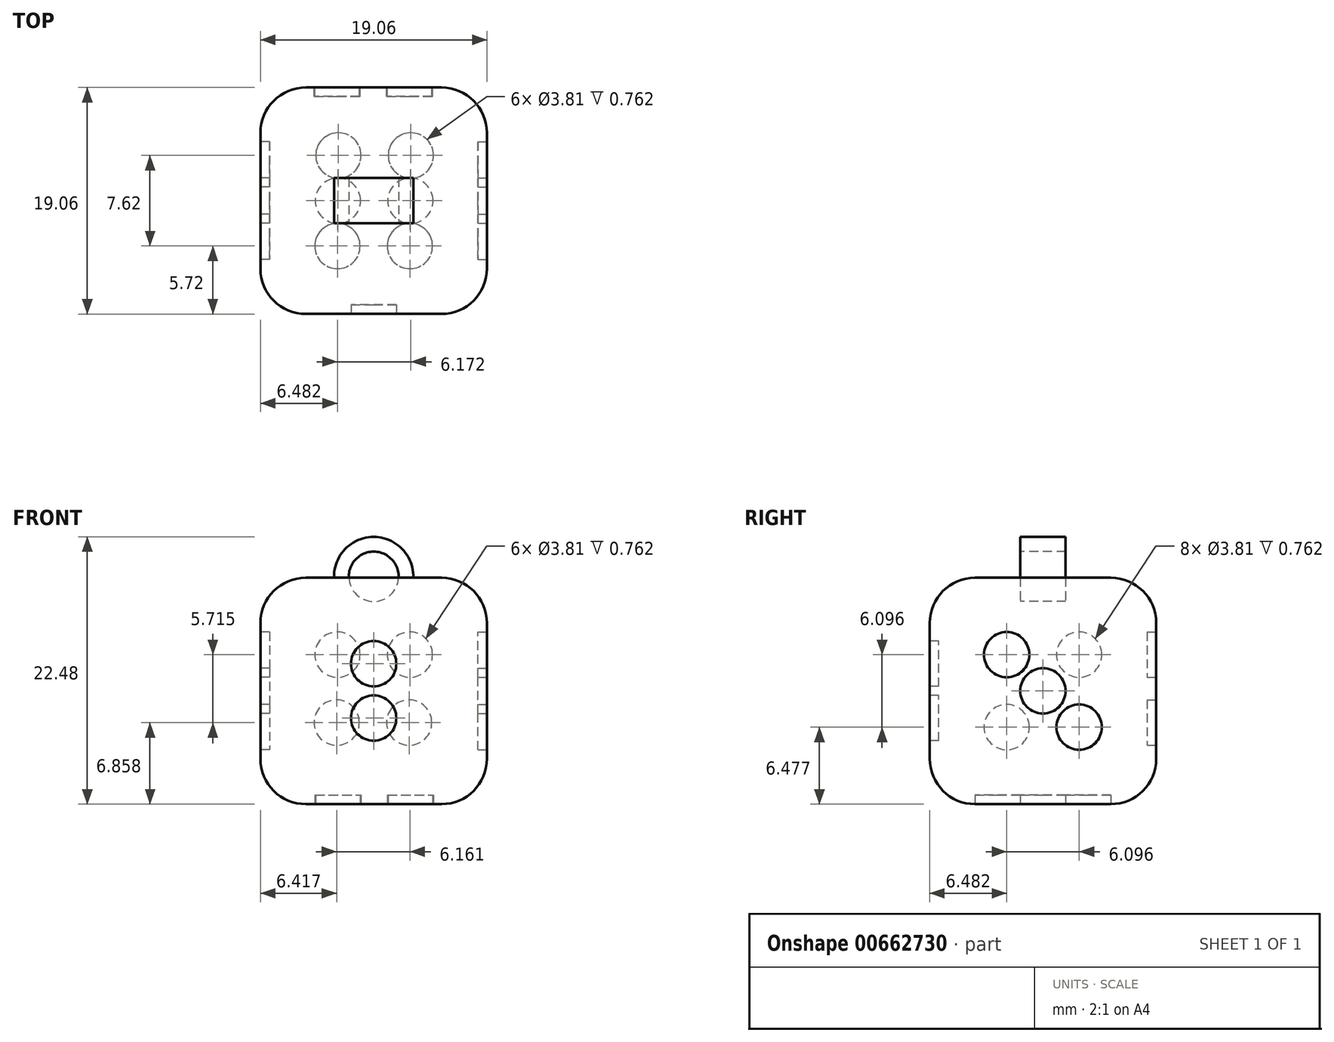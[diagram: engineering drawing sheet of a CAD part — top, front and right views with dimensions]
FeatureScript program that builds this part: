
annotation { "Feature Type Name" : "Feature", "Feature Type Description" : "" }
export const myFeature = defineFeature(function(context is Context, id is Id, definition is map)
    precondition{}
    {
        {
            var Q0;
            Q0=qCreatedBy(makeId("Top.planeOp"),FACE);
            var sketch = newSketch(context, id + "F0", { "sketchPlane" : qUnion([Q0])});
            skLineSegment(sketch, "E0.bottom", {"start": v(6.35, -6.35) * mm, "end": v(-6.35, -6.35) * mm});
            skLineSegment(sketch, "E0.top", {"start": v(6.35, 6.35) * mm, "end": v(-6.35, 6.35) * mm});
            skLineSegment(sketch, "E0.left", {"start": v(6.35, -6.35) * mm, "end": v(6.35, 6.35) * mm});
            skLineSegment(sketch, "E0.right", {"start": v(-6.35, -6.35) * mm, "end": v(-6.35, 6.35) * mm});
            skPoint(sketch, "E0.middle", {"position": v(0, 0) * mm});
            skSolve(sketch);
        }
        {
            var Q0;
            Q0 = qSketchRegion(id + "F0", true);
            extrude(context, id + "F1", {"entities" : qUnion([Q0]), "depth" : 12.7 * mm, "offsetDistance" : 25.4 * mm});
        }
        {
            var Q0;
            Q0=makeQuery(id+"F1.opExtrude","CAP_FACE",FACE,{"disambiguationData":[OSD([sQuery(id+"F0.wireOp",EDGE,"E0.bottom"),sQuery(id+"F0.wireOp",EDGE,"E0.top"),sQuery(id+"F0.wireOp",EDGE,"E0.left"),sQuery(id+"F0.wireOp",EDGE,"E0.right")])],"isStart":false});
            fillet(context, id + "F2", {"entities" : qUnion([Q0]), "radius" : 2.54 * mm, "tangentPropagation" : true, "allowEdgeOverflow" : false});
        }
        {
            var Q0;
            Q0=makeQuery(id+"F1.opExtrude","SWEPT_FACE",FACE,{"disambiguationData":[OSD([sQuery(id+"F0.wireOp",EDGE,"E0.bottom")])]});
            fillet(context, id + "F3", {"entities" : qUnion([Q0]), "radius" : 2.54 * mm, "tangentPropagation" : true, "allowEdgeOverflow" : false});
        }
        {
            var Q0;
            Q0=makeQuery(id+"F1.opExtrude","SWEPT_FACE",FACE,{"disambiguationData":[OSD([sQuery(id+"F0.wireOp",EDGE,"E0.left")])]});
            fillet(context, id + "F4", {"entities" : qUnion([Q0]), "radius" : 2.54 * mm, "tangentPropagation" : true, "allowEdgeOverflow" : false});
        }
        {
            var Q0;
            Q0=makeQuery(id+"F1.opExtrude","SWEPT_FACE",FACE,{"disambiguationData":[OSD([sQuery(id+"F0.wireOp",EDGE,"E0.top")])]});
            fillet(context, id + "F5", {"entities" : qUnion([Q0]), "radius" : 2.54 * mm, "tangentPropagation" : true, "allowEdgeOverflow" : false});
        }
        {
            var Q0;
            Q0=makeQuery(id+"F1.opExtrude","SWEPT_FACE",FACE,{"disambiguationData":[OSD([sQuery(id+"F0.wireOp",EDGE,"E0.right")])]});
            fillet(context, id + "F6", {"entities" : qUnion([Q0]), "radius" : 2.54 * mm, "tangentPropagation" : true, "allowEdgeOverflow" : false});
        }
        {
            var Q0;
            Q0=qCreatedBy(makeId("Front.planeOp"),FACE);
            var sketch = newSketch(context, id + "F7", { "sketchPlane" : qUnion([Q0])});
            skCircle(sketch, "E1", {"center": v(0, 12.76) * mm, "radius": 2.22 * mm});
            skSolve(sketch);
        }
        {
            var Q0;
            Q0 = qSketchRegion(id + "F7", true);
            extrude(context, id + "F8", {"entities" : qUnion([Q0]), "operationType" : NewBodyOperationType.ADD, "endBound" : BoundingType.SYMMETRIC, "depth" : 2.54 * mm, "offsetDistance" : 25.4 * mm});
        }
        {
            var Q0;
            Q0=makeQuery(id+"F8.opExtrude","CAP_FACE",FACE,{"disambiguationData":[OSD([sQuery(id+"F7.wireOp",EDGE,"E1")])],"isStart":false});
            var sketch = newSketch(context, id + "F9", { "sketchPlane" : qUnion([Q0])});
            skCircle(sketch, "E2", {"center": v(0, 12.76) * mm, "radius": 1.4 * mm});
            skSolve(sketch);
        }
        {
            var Q0;
            Q0 = qSketchRegion(id + "F9", true);
            extrude(context, id + "F10", {"entities" : qUnion([Q0]), "operationType" : NewBodyOperationType.REMOVE, "oppositeDirection" : true, "depth" : 2.54 * mm, "offsetDistance" : 25.4 * mm});
        }
        {
            var Q0;
            Q0=makeQuery(id+"F1.opExtrude","SWEPT_FACE",FACE,{"disambiguationData":[OSD([sQuery(id+"F0.wireOp",EDGE,"E0.bottom")])]});
            var sketch = newSketch(context, id + "F11", { "sketchPlane" : qUnion([Q0])});
            skCircle(sketch, "E3", {"center": v(0, 4.83) * mm, "radius": 1.27 * mm});
            skPoint(sketch, "E3.centerSnap0", {"position": v(0, 2.54) * mm});
            skCircle(sketch, "E4", {"center": v(0, 7.87) * mm, "radius": 1.27 * mm});
            skPoint(sketch, "E4.centerSnap0", {"position": v(0, 10.16) * mm});
            skSolve(sketch);
        }
        {
            var Q0;
            Q0 = qSketchRegion(id + "F11", true);
            extrude(context, id + "F12", {"entities" : qUnion([Q0]), "operationType" : NewBodyOperationType.REMOVE, "oppositeDirection" : true, "depth" : 0.5 * mm, "offsetDistance" : 25.4 * mm});
        }
        {
            var Q0;
            Q0=makeQuery(id+"F1.opExtrude","SWEPT_FACE",FACE,{"disambiguationData":[OSD([sQuery(id+"F0.wireOp",EDGE,"E0.left")])]});
            var sketch = newSketch(context, id + "F13", { "sketchPlane" : qUnion([Q0])});
            skLineSegment(sketch, "E5", {"start": v(-3.8, 10.16) * mm, "end": v(3.81, 2.54) * mm});
            skLineSegment(sketch, "E6", {"start": v(-3.8, 2.54) * mm, "end": v(3.81, 10.16) * mm});
            skCircle(sketch, "E7", {"center": v(0, 6.35) * mm, "radius": 1.27 * mm});
            skCircle(sketch, "E8", {"center": v(-2.03, 8.38) * mm, "radius": 1.27 * mm});
            skCircle(sketch, "E9", {"center": v(2.03, 4.32) * mm, "radius": 1.27 * mm});
            skSolve(sketch);
        }
        {
            var Q0;
            Q0 = qSketchRegion(id + "F13", true);
            extrude(context, id + "F14", {"entities" : qUnion([Q0]), "operationType" : NewBodyOperationType.REMOVE, "oppositeDirection" : true, "depth" : 0.5 * mm, "offsetDistance" : 25.4 * mm});
        }
        {
            var Q0;
            Q0=makeQuery(id+"F1.opExtrude","SWEPT_FACE",FACE,{"disambiguationData":[OSD([sQuery(id+"F0.wireOp",EDGE,"E0.top")])]});
            var sketch = newSketch(context, id + "F15", { "sketchPlane" : qUnion([Q0])});
            skCircle(sketch, "E10", {"center": v(-2.03, 8.38) * mm, "radius": 1.27 * mm});
            skCircle(sketch, "E11.1.0.0", {"center": v(2.03, 8.38) * mm, "radius": 1.27 * mm});
            skLineSegment(sketch, "E11.direction1", {"start": v(-2.03, 8.38) * mm, "end": v(2.03, 8.38) * mm, "construction": true});
            skCircle(sketch, "E12.1.0.0", {"center": v(-1.99, 4.57) * mm, "radius": 1.27 * mm});
            skCircle(sketch, "E12.1.0.1", {"center": v(2.08, 4.57) * mm, "radius": 1.27 * mm});
            skLineSegment(sketch, "E12.direction1", {"start": v(-2.03, 8.38) * mm, "end": v(-1.99, 4.57) * mm, "construction": true});
            skSolve(sketch);
        }
        {
            var Q0;
            Q0 = qSketchRegion(id + "F15", true);
            extrude(context, id + "F16", {"entities" : qUnion([Q0]), "operationType" : NewBodyOperationType.REMOVE, "oppositeDirection" : true, "depth" : 0.5 * mm, "offsetDistance" : 25.4 * mm});
        }
        {
            var Q0;
            Q0=makeQuery(id+"F1.opExtrude","SWEPT_FACE",FACE,{"disambiguationData":[OSD([sQuery(id+"F0.wireOp",EDGE,"E0.right")])]});
            var sketch = newSketch(context, id + "F17", { "sketchPlane" : qUnion([Q0])});
            skLineSegment(sketch, "E13", {"start": v(-3.81, 10.16) * mm, "end": v(3.8, 2.54) * mm});
            skLineSegment(sketch, "E14", {"start": v(-3.81, 2.54) * mm, "end": v(3.81, 10.16) * mm});
            skCircle(sketch, "E15", {"center": v(0, 6.35) * mm, "radius": 1.27 * mm});
            skCircle(sketch, "E16", {"center": v(-2.03, 8.38) * mm, "radius": 1.27 * mm});
            skCircle(sketch, "E17.1.0.0", {"center": v(2.03, 8.38) * mm, "radius": 1.27 * mm});
            skLineSegment(sketch, "E17.direction1", {"start": v(-2.03, 8.38) * mm, "end": v(2.03, 8.38) * mm, "construction": true});
            skCircle(sketch, "E18", {"center": v(-2.03, 4.32) * mm, "radius": 1.27 * mm});
            skCircle(sketch, "E19.1.0.0", {"center": v(2.03, 4.32) * mm, "radius": 1.27 * mm});
            skLineSegment(sketch, "E19.direction1", {"start": v(-2.03, 4.32) * mm, "end": v(2.03, 4.32) * mm, "construction": true});
            skSolve(sketch);
        }
        {
            var Q0;
            Q0 = qSketchRegion(id + "F17", true);
            extrude(context, id + "F18", {"entities" : qUnion([Q0]), "operationType" : NewBodyOperationType.REMOVE, "oppositeDirection" : true, "depth" : 0.5 * mm, "offsetDistance" : 25.4 * mm});
        }
        {
            var Q0;
            Q0=makeQuery(id+"F1.opExtrude","CAP_FACE",FACE,{"disambiguationData":[OSD([sQuery(id+"F0.wireOp",EDGE,"E0.bottom"),sQuery(id+"F0.wireOp",EDGE,"E0.top"),sQuery(id+"F0.wireOp",EDGE,"E0.left"),sQuery(id+"F0.wireOp",EDGE,"E0.right")])],"isStart":true});
            var sketch = newSketch(context, id + "F19", { "sketchPlane" : qUnion([Q0])});
            skCircle(sketch, "E20", {"center": v(-2.03, 2.54) * mm, "radius": 1.27 * mm});
            skCircle(sketch, "E21.1.0.0", {"center": v(2.03, 2.54) * mm, "radius": 1.27 * mm});
            skLineSegment(sketch, "E21.direction1", {"start": v(-2.03, 2.54) * mm, "end": v(2.03, 2.54) * mm, "construction": true});
            skCircle(sketch, "E22.1.0.0", {"center": v(-2, 0) * mm, "radius": 1.27 * mm});
            skCircle(sketch, "E22.1.0.1", {"center": v(2.06, 0) * mm, "radius": 1.27 * mm});
            skCircle(sketch, "E22.2.0.0", {"center": v(-1.98, -2.54) * mm, "radius": 1.27 * mm});
            skCircle(sketch, "E22.2.0.1", {"center": v(2.08, -2.54) * mm, "radius": 1.27 * mm});
            skLineSegment(sketch, "E22.direction1", {"start": v(-2.03, 2.54) * mm, "end": v(-2, 0) * mm, "construction": true});
            skSolve(sketch);
        }
        {
            var Q0;
            Q0 = qSketchRegion(id + "F19", true);
            extrude(context, id + "F20", {"entities" : qUnion([Q0]), "operationType" : NewBodyOperationType.REMOVE, "oppositeDirection" : true, "depth" : 0.5 * mm, "offsetDistance" : 25.4 * mm});
        }
        {
            var Q0;
            Q0=makeQuery(id+"F1.opExtrude","SWEPT_BODY",BODY,{"disambiguationData":[OSD([sQuery(id+"F0.wireOp",EDGE,"E0.bottom"),sQuery(id+"F0.wireOp",EDGE,"E0.top"),sQuery(id+"F0.wireOp",EDGE,"E0.left"),sQuery(id+"F0.wireOp",EDGE,"E0.right")])]});
            var Q1;
            Q1=qCreatedBy(makeId("Origin.pointOp"),VERTEX);
            transform(context, id + "F21", {"entities" : qUnion([Q0]), "transformType" : TransformType.SCALE_UNIFORMLY, "scale" : 1.5, "scalePoint" : qUnion([Q1]), "makeCopy" : false});
        }
    });
